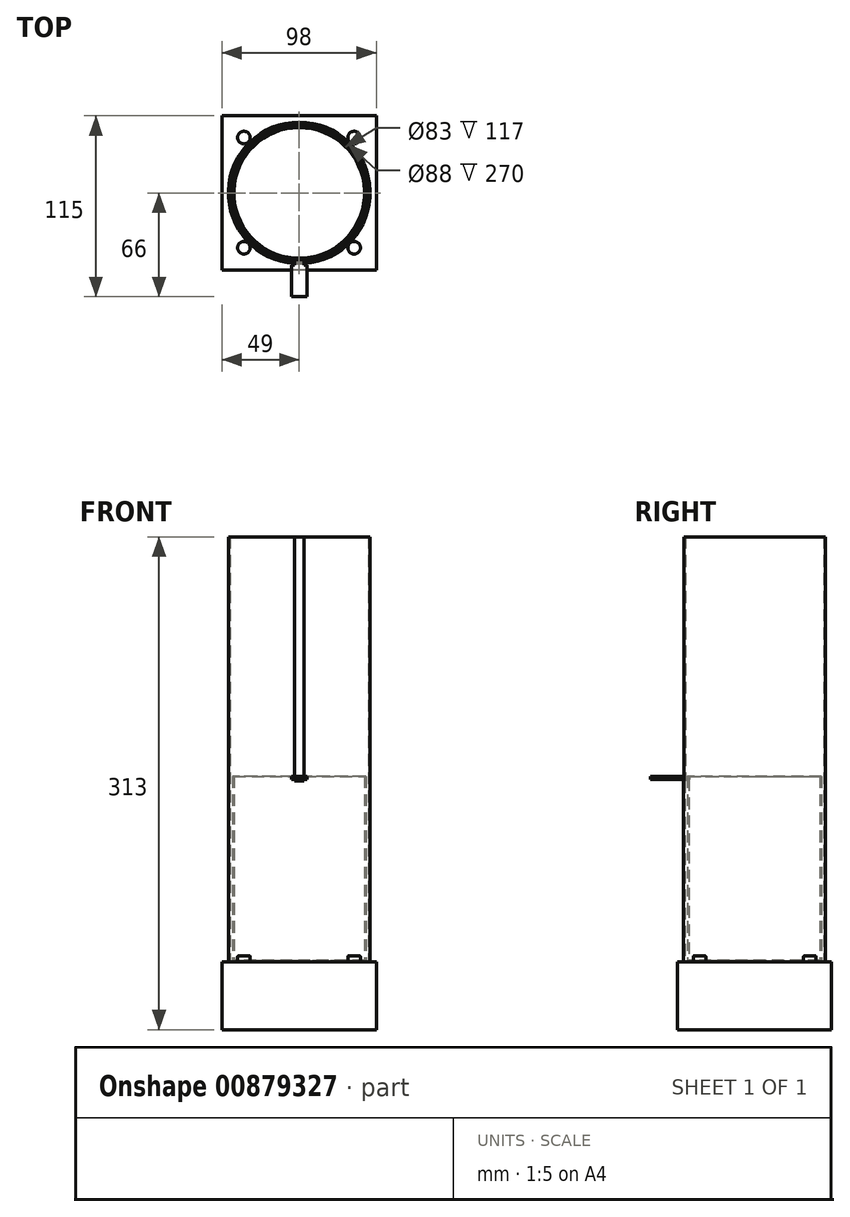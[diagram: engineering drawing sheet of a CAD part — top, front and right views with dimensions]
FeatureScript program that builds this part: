
annotation { "Feature Type Name" : "Feature", "Feature Type Description" : "" }
export const myFeature = defineFeature(function(context is Context, id is Id, definition is map)
    precondition{}
    {
        {
            var Q0;
            Q0=qCreatedBy(makeId("Top.planeOp"),FACE);
            var sketch = newSketch(context, id + "F0", { "sketchPlane" : qUnion([Q0])});
            skCircle(sketch, "E0", {"center": v(0, 0) * mm, "radius": 45 * mm});
            skCircle(sketch, "E1", {"center": v(0, 0) * mm, "radius": 44 * mm});
            skSolve(sketch);
        }
        {
            var Q0;
            Q0=makeQuery(id+"F0.imprint","IMPRINT",FACE,{"disambiguationData":[TD([[makeQuery(id+"F0.imprint","IMPRINT",EDGE,{"derivedFrom":sQuery(id+"F0.wireOp",EDGE,"E0")}),1.0]])]});
            extrude(context, id + "F1", {"entities" : qUnion([Q0]), "depth" : 270 * mm, "offsetDistance" : 25 * mm});
        }
        {
            var Q0;
            Q0=qCreatedBy(makeId("Front.planeOp"),FACE);
            var sketch = newSketch(context, id + "F2", { "sketchPlane" : qUnion([Q0])});
            skLineSegment(sketch, "E2", {"start": v(0, 0) * mm, "end": v(0, 115) * mm, "construction": true});
            skLineSegment(sketch, "E3", {"start": v(0, 115) * mm, "end": v(3, 115) * mm, "construction": true});
            skLineSegment(sketch, "E4.bottom", {"start": v(3, 115) * mm, "end": v(-3, 115) * mm});
            skLineSegment(sketch, "E4.top", {"start": v(3, 270) * mm, "end": v(-3, 270) * mm});
            skLineSegment(sketch, "E4.left", {"start": v(3, 115) * mm, "end": v(3, 270) * mm});
            skLineSegment(sketch, "E4.right", {"start": v(-3, 115) * mm, "end": v(-3, 270) * mm});
            skSolve(sketch);
        }
        {
            var Q0;
            Q0=makeQuery(id+"F2.imprint","IMPRINT",FACE,{"disambiguationData":[TD([[makeQuery(id+"F2.imprint","IMPRINT",EDGE,{"derivedFrom":sQuery(id+"F2.wireOp",EDGE,"E4.bottom")}),-1.0]])]});
            extrude(context, id + "F3", {"entities" : qUnion([Q0]), "operationType" : NewBodyOperationType.REMOVE, "depth" : 55 * mm, "offsetDistance" : 25 * mm});
        }
        {
            var Q0;
            Q0=qCreatedBy(makeId("Top.planeOp"),FACE);
            var sketch = newSketch(context, id + "F4", { "sketchPlane" : qUnion([Q0])});
            skCircle(sketch, "E5", {"center": v(0, 0) * mm, "radius": 42.5 * mm});
            skSolve(sketch);
        }
        {
            var Q0;
            Q0=makeQuery(id+"F4.imprint","IMPRINT",FACE,{"disambiguationData":[TD([[makeQuery(id+"F4.imprint","IMPRINT",EDGE,{"derivedFrom":sQuery(id+"F4.wireOp",EDGE,"E5")}),1.0]])]});
            extrude(context, id + "F5", {"entities" : qUnion([Q0]), "depth" : 118 * mm, "offsetDistance" : 25 * mm});
        }
        {
            var Q0;
            Q0=makeQuery(id+"F5.opExtrude","CAP_FACE",FACE,{"disambiguationData":[OSD([sQuery(id+"F4.wireOp",EDGE,"E5")])],"isStart":false});
            shell(context, id + "F6", {"entities" : qUnion([Q0]), "thickness" : 1 * mm});
        }
        {
            var Q0;
            Q0=qCreatedBy(makeId("Front.planeOp"),FACE);
            var sketch = newSketch(context, id + "F7", { "sketchPlane" : qUnion([Q0])});
            skLineSegment(sketch, "E6", {"start": v(0, 0) * mm, "end": v(0, 116) * mm, "construction": true});
            skLineSegment(sketch, "E7", {"start": v(0, 116) * mm, "end": v(3, 116) * mm});
            skLineSegment(sketch, "E8", {"start": v(3, 116) * mm, "end": v(3, 118) * mm});
            skLineSegment(sketch, "E9", {"start": v(3, 118) * mm, "end": v(-3, 118) * mm});
            skLineSegment(sketch, "E10", {"start": v(-3, 118) * mm, "end": v(-3, 116) * mm});
            skLineSegment(sketch, "E11", {"start": v(-3, 116) * mm, "end": v(0, 116) * mm});
            skSolve(sketch);
        }
        {
            var Q0;
            Q0=makeQuery(id+"F7.imprint","IMPRINT",FACE,{"disambiguationData":[TD([[makeQuery(id+"F7.imprint","IMPRINT",EDGE,{"derivedFrom":sQuery(id+"F7.wireOp",EDGE,"E7")}),1.0]])]});
            extrude(context, id + "F8", {"entities" : qUnion([Q0]), "depth" : 46 * mm, "offsetDistance" : 25 * mm});
        }
        {
            var Q0;
            Q0=makeQuery(id+"F8.opExtrude","CAP_FACE",FACE,{"disambiguationData":[OSD([sQuery(id+"F7.wireOp",EDGE,"E7"),sQuery(id+"F7.wireOp",EDGE,"E8"),sQuery(id+"F7.wireOp",EDGE,"E9"),sQuery(id+"F7.wireOp",EDGE,"E10"),sQuery(id+"F7.wireOp",EDGE,"E11")])],"isStart":true});
            extrude(context, id + "F9", {"entities" : qUnion([Q0]), "operationType" : NewBodyOperationType.REMOVE, "oppositeDirection" : true, "depth" : 42 * mm, "offsetDistance" : 25 * mm});
        }
        {
            var Q0;
            Q0=makeQuery(id+"F8.opExtrude","CAP_FACE",FACE,{"disambiguationData":[OSD([sQuery(id+"F7.wireOp",EDGE,"E7"),sQuery(id+"F7.wireOp",EDGE,"E8"),sQuery(id+"F7.wireOp",EDGE,"E9"),sQuery(id+"F7.wireOp",EDGE,"E10"),sQuery(id+"F7.wireOp",EDGE,"E11")])],"isStart":false});
            var sketch = newSketch(context, id + "F10", { "sketchPlane" : qUnion([Q0])});
            skLineSegment(sketch, "E12", {"start": v(3, 118) * mm, "end": v(5, 118) * mm});
            skLineSegment(sketch, "E13", {"start": v(5, 118) * mm, "end": v(5, 116) * mm});
            skLineSegment(sketch, "E14", {"start": v(5, 116) * mm, "end": v(-5, 116) * mm});
            skLineSegment(sketch, "E15", {"start": v(-5, 116) * mm, "end": v(-5, 118) * mm});
            skLineSegment(sketch, "E16", {"start": v(-5, 118) * mm, "end": v(3, 118) * mm});
            skSolve(sketch);
        }
        {
            var Q0;
            Q0 = qSketchRegion(id + "F10", true);
            extrude(context, id + "F11", {"entities" : qUnion([Q0]), "operationType" : NewBodyOperationType.ADD, "depth" : 20 * mm, "offsetDistance" : 25 * mm});
        }
        {
            var Q0;
            Q0=qCreatedBy(makeId("Top.planeOp"),FACE);
            var sketch = newSketch(context, id + "F12", { "sketchPlane" : qUnion([Q0])});
            skLineSegment(sketch, "E17", {"start": v(0, 0) * mm, "end": v(-49, 0) * mm, "construction": true});
            skLineSegment(sketch, "E18", {"start": v(-49, 0) * mm, "end": v(-49, 49) * mm});
            skLineSegment(sketch, "E19", {"start": v(-49, 49) * mm, "end": v(49, 49) * mm});
            skLineSegment(sketch, "E20", {"start": v(49, 49) * mm, "end": v(49, -49) * mm});
            skLineSegment(sketch, "E21", {"start": v(49, -49) * mm, "end": v(-49, -49) * mm});
            skLineSegment(sketch, "E22", {"start": v(-49, -49) * mm, "end": v(-49, 0) * mm});
            skSolve(sketch);
        }
        {
            var Q0;
            Q0=makeQuery(id+"F12.imprint","IMPRINT",FACE,{"disambiguationData":[TD([[makeQuery(id+"F12.imprint","IMPRINT",EDGE,{"derivedFrom":sQuery(id+"F12.wireOp",EDGE,"E18")}),-1.0]])]});
            extrude(context, id + "F13", {"entities" : qUnion([Q0]), "oppositeDirection" : true, "depth" : 43 * mm, "offsetDistance" : 25 * mm});
        }
        {
            var Q0;
            Q0=makeQuery(id+"F13.opExtrude","CAP_FACE",FACE,{"disambiguationData":[OSD([sQuery(id+"F12.wireOp",EDGE,"E18"),sQuery(id+"F12.wireOp",EDGE,"E19"),sQuery(id+"F12.wireOp",EDGE,"E20"),sQuery(id+"F12.wireOp",EDGE,"E21"),sQuery(id+"F12.wireOp",EDGE,"E22")])],"isStart":true});
            var sketch = newSketch(context, id + "F14", { "sketchPlane" : qUnion([Q0])});
            skLineSegment(sketch, "E23", {"start": v(49, 0) * mm, "end": v(49, -49) * mm, "construction": true});
            skLineSegment(sketch, "E24", {"start": v(49, -49) * mm, "end": v(0, -49) * mm, "construction": true});
            skLineSegment(sketch, "E25", {"start": v(49, -49) * mm, "end": v(34.86, -34.86) * mm, "construction": true});
            skCircle(sketch, "E26", {"center": v(34.86, -34.86) * mm, "radius": 4 * mm});
            skCircle(sketch, "E27.0.1.0", {"center": v(34.86, 35.14) * mm, "radius": 4 * mm});
            skCircle(sketch, "E27.1.0.0", {"center": v(-35.14, -34.86) * mm, "radius": 4 * mm});
            skCircle(sketch, "E27.1.1.0", {"center": v(-35.14, 35.14) * mm, "radius": 4 * mm});
            skLineSegment(sketch, "E27.direction1", {"start": v(34.86, -34.86) * mm, "end": v(-35.14, -34.86) * mm, "construction": true});
            skLineSegment(sketch, "E27.direction2", {"start": v(34.86, -34.86) * mm, "end": v(34.86, 35.14) * mm, "construction": true});
            skSolve(sketch);
        }
        {
            var Q0;
            Q0=makeQuery(id+"F14.imprint","IMPRINT",FACE,{"disambiguationData":[TD([[makeQuery(id+"F14.imprint","IMPRINT",EDGE,{"derivedFrom":sQuery(id+"F14.wireOp",EDGE,"E27.0.1.0")}),1.0]])]});
            var Q1;
            Q1=makeQuery(id+"F14.imprint","IMPRINT",FACE,{"disambiguationData":[TD([[makeQuery(id+"F14.imprint","IMPRINT",EDGE,{"derivedFrom":sQuery(id+"F14.wireOp",EDGE,"E27.1.1.0")}),1.0]])]});
            var Q2;
            Q2=makeQuery(id+"F14.imprint","IMPRINT",FACE,{"disambiguationData":[TD([[makeQuery(id+"F14.imprint","IMPRINT",EDGE,{"derivedFrom":sQuery(id+"F14.wireOp",EDGE,"E26")}),1.0]])]});
            var Q3;
            Q3=makeQuery(id+"F14.imprint","IMPRINT",FACE,{"disambiguationData":[TD([[makeQuery(id+"F14.imprint","IMPRINT",EDGE,{"derivedFrom":sQuery(id+"F14.wireOp",EDGE,"E27.1.0.0")}),1.0]])]});
            extrude(context, id + "F15", {"entities" : qUnion([Q0, Q1, Q2, Q3]), "operationType" : NewBodyOperationType.ADD, "depth" : 4 * mm, "offsetDistance" : 25 * mm});
        }
        {
            var Q0;
            Q0=makeQuery(id+"F15.opExtrude","CAP_FACE",FACE,{"disambiguationData":[OSD([sQuery(id+"F14.wireOp",EDGE,"E27.1.1.0")])],"isStart":false});
            var Q1;
            Q1=makeQuery(id+"F15.opExtrude","CAP_FACE",FACE,{"disambiguationData":[OSD([sQuery(id+"F14.wireOp",EDGE,"E27.1.0.0")])],"isStart":false});
            var Q2;
            Q2=makeQuery(id+"F15.opExtrude","CAP_FACE",FACE,{"disambiguationData":[OSD([sQuery(id+"F14.wireOp",EDGE,"E26")])],"isStart":false});
            var Q3;
            Q3=makeQuery(id+"F15.opExtrude","CAP_FACE",FACE,{"disambiguationData":[OSD([sQuery(id+"F14.wireOp",EDGE,"E27.0.1.0")])],"isStart":false});
            fillet(context, id + "F16", {"entities" : qUnion([Q0, Q1, Q2, Q3]), "radius" : 0.8 * mm, "tangentPropagation" : true, "allowEdgeOverflow" : false});
        }
    });
